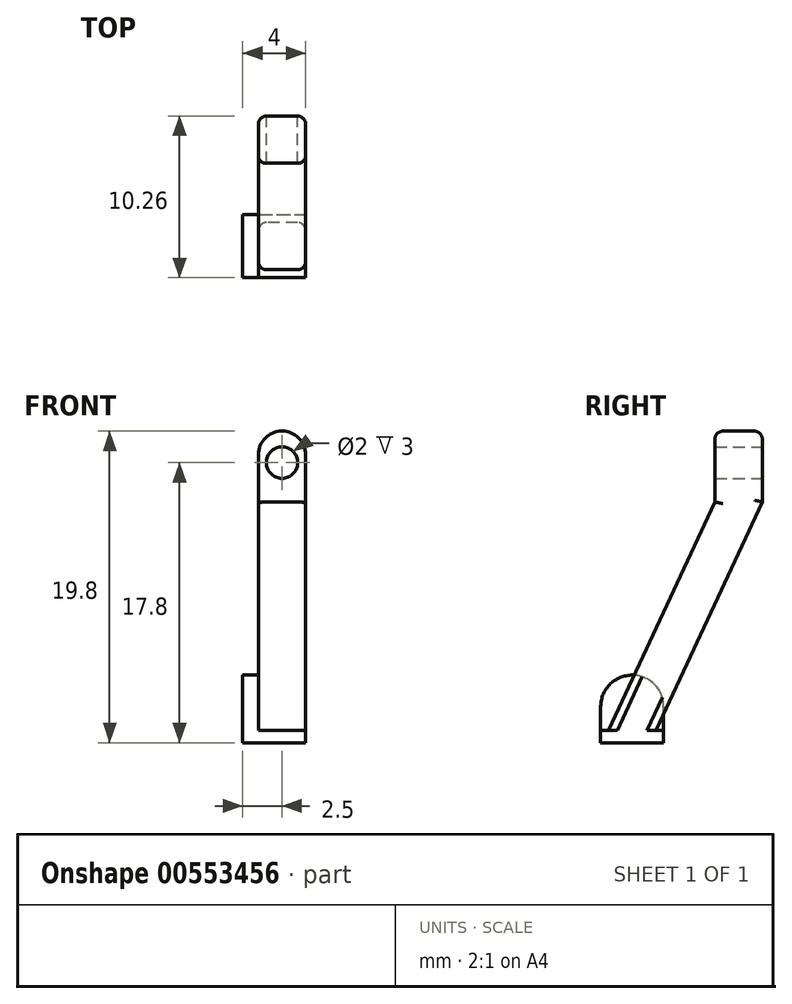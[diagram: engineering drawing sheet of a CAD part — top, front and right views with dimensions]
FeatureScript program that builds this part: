
annotation { "Feature Type Name" : "Feature", "Feature Type Description" : "" }
export const myFeature = defineFeature(function(context is Context, id is Id, definition is map)
    precondition{}
    {
        {
            var Q0;
            Q0=qCreatedBy(makeId("Top.planeOp"),FACE);
            var sketch = newSketch(context, id + "F0", { "sketchPlane" : qUnion([Q0])});
            skLineSegment(sketch, "E0.bottom", {"start": v(0, 0) * mm, "end": v(4, 0) * mm});
            skLineSegment(sketch, "E0.top", {"start": v(0, 4) * mm, "end": v(4, 4) * mm});
            skLineSegment(sketch, "E0.left", {"start": v(0, 0) * mm, "end": v(0, 4) * mm});
            skLineSegment(sketch, "E0.right", {"start": v(4, 0) * mm, "end": v(4, 4) * mm});
            skSolve(sketch);
        }
        {
            var Q0;
            Q0 = qSketchRegion(id + "F0", true);
            extrude(context, id + "F1", {"entities" : qUnion([Q0]), "depth" : 0.8 * mm, "offsetDistance" : 25 * mm});
        }
        {
            var Q0;
            Q0=qCreatedBy(makeId("Right.planeOp"),FACE);
            cPlane(context, id + "F2", {"entities" : qUnion([Q0]), "cplaneType" : CPlaneType.OFFSET, "offset" : 2.5 * mm, "width" : 150 * mm, "height" : 150 * mm});
        }
        {
            var Q0;
            Q0=qCreatedBy(id+"F2.planeOp",FACE);
            var sketch = newSketch(context, id + "F3", { "sketchPlane" : qUnion([Q0])});
            skLineSegment(sketch, "E1", {"start": v(3.5, 0.8) * mm, "end": v(10.26, 15.3) * mm});
            skLineSegment(sketch, "E2", {"start": v(7.26, 15.3) * mm, "end": v(0.5, 0.8) * mm});
            skLineSegment(sketch, "E3", {"start": v(0.5, 0.8) * mm, "end": v(3.5, 0.8) * mm});
            skLineSegment(sketch, "E4", {"start": v(7.26, 15.3) * mm, "end": v(7.26, 19.8) * mm});
            skLineSegment(sketch, "E5", {"start": v(7.26, 19.8) * mm, "end": v(10.26, 19.8) * mm});
            skLineSegment(sketch, "E6", {"start": v(10.26, 19.8) * mm, "end": v(10.26, 15.3) * mm});
            skLineSegment(sketch, "E7", {"start": v(7.26, 15.3) * mm, "end": v(15, 15.3) * mm, "construction": true});
            skSolve(sketch);
        }
        {
            var Q0;
            Q0 = qSketchRegion(id + "F3", true);
            extrude(context, id + "F4", {"entities" : qUnion([Q0]), "operationType" : NewBodyOperationType.ADD, "endBound" : BoundingType.SYMMETRIC, "depth" : 3 * mm, "offsetDistance" : 25 * mm});
        }
        {
            var Q0;
            Q0=makeQuery(id+"F4.opExtrude","SWEPT_FACE",FACE,{"disambiguationData":[OSD([sQuery(id+"F3.wireOp",EDGE,"E6")])]});
            var sketch = newSketch(context, id + "F5", { "sketchPlane" : qUnion([Q0])});
            skCircle(sketch, "E8", {"center": v(-2.5, 17.8) * mm, "radius": 1 * mm});
            skSolve(sketch);
        }
        {
            var Q0;
            Q0 = qSketchRegion(id + "F5", true);
            extrude(context, id + "F6", {"entities" : qUnion([Q0]), "operationType" : NewBodyOperationType.REMOVE, "endBound" : BoundingType.THROUGH_ALL, "oppositeDirection" : true, "depth" : 25 * mm, "offsetDistance" : 25 * mm});
        }
        {
            var Q0;
            Q0=makeQuery(id+"F4.opExtrude","CAP_EDGE",EDGE,{"disambiguationData":[OSD([sQuery(id+"F3.wireOp",EDGE,"E5")])],"isStart":true});
            var Q1;
            Q1=makeQuery(id+"F4.opExtrude","CAP_EDGE",EDGE,{"disambiguationData":[OSD([sQuery(id+"F3.wireOp",EDGE,"E5")])],"isStart":false});
            fillet(context, id + "F7", {"entities" : qUnion([Q0, Q1]), "radius" : 1.5 * mm, "tangentPropagation" : true, "allowEdgeOverflow" : false});
        }
        {
            var Q0;
            Q0=makeQuery(id+"F4.opExtrude","CAP_EDGE",EDGE,{"disambiguationData":[OSD([sQuery(id+"F3.wireOp",EDGE,"E1")])],"isStart":true});
            var Q1;
            Q1=makeQuery(id+"F4.opExtrude","CAP_EDGE",EDGE,{"disambiguationData":[OSD([sQuery(id+"F3.wireOp",EDGE,"E6")])],"isStart":true});
            var Q2;
            Q2=makeQuery(id+"F7.opFillet","BLEND_EDGE",EDGE,{"blendedFrom":[makeQuery(id+"F4.opExtrude","CAP_EDGE",EDGE,{"disambiguationData":[OSD([sQuery(id+"F3.wireOp",EDGE,"E5")])],"isStart":false}),makeQuery(id+"F4.opExtrude","SWEPT_FACE",FACE,{"disambiguationData":[OSD([sQuery(id+"F3.wireOp",EDGE,"E6")])]})],"blendedInto":[makeQuery(id+"F4.opExtrude","SWEPT_FACE",FACE,{"disambiguationData":[OSD([sQuery(id+"F3.wireOp",EDGE,"E6")])]})]});
            var Q3;
            Q3=makeQuery(id+"F4.opExtrude","CAP_EDGE",EDGE,{"disambiguationData":[OSD([sQuery(id+"F3.wireOp",EDGE,"E1")])],"isStart":false});
            var Q4;
            Q4=makeQuery(id+"F4.opExtrude","CAP_EDGE",EDGE,{"disambiguationData":[OSD([sQuery(id+"F3.wireOp",EDGE,"E2")])],"isStart":true});
            var Q5;
            Q5=makeQuery(id+"F4.opExtrude","CAP_EDGE",EDGE,{"disambiguationData":[OSD([sQuery(id+"F3.wireOp",EDGE,"E4")])],"isStart":true});
            var Q6;
            Q6=makeQuery(id+"F4.opExtrude","CAP_EDGE",EDGE,{"disambiguationData":[OSD([sQuery(id+"F3.wireOp",EDGE,"E2")])],"isStart":false});
            fillet(context, id + "F8", {"entities" : qUnion([Q0, Q1, Q2, Q3, Q4, Q5, Q6]), "radius" : 0.5 * mm, "tangentPropagation" : true, "allowEdgeOverflow" : false});
        }
        {
            var Q0;
            Q0=makeQuery(id+"F1.opExtrude","SWEPT_FACE",FACE,{"disambiguationData":[OSD([sQuery(id+"F0.wireOp",EDGE,"E0.left")])]});
            var sketch = newSketch(context, id + "F9", { "sketchPlane" : qUnion([Q0])});
            skLineSegment(sketch, "E9.bottom", {"start": v(-4, 0.8) * mm, "end": v(0, 0.8) * mm});
            skLineSegment(sketch, "E9.top", {"start": v(-2, 4.3) * mm, "end": v(-2, 4.3) * mm});
            skLineSegment(sketch, "E9.left", {"start": v(-4, 0.8) * mm, "end": v(-4, 2.3) * mm});
            skLineSegment(sketch, "E9.right", {"start": v(0, 0.8) * mm, "end": v(0, 2.3) * mm});
            skPoint(sketch, "E10.visualSharp", {"position": v(-4, 4.3) * mm});
            skArc(sketch, "E10.filletArc", {"start": v(-2, 4.3) * mm, "mid": v(-3.41, 3.71) * mm, "end": v(-4, 2.3) * mm});
            skPoint(sketch, "E11.visualSharp", {"position": v(0, 4.3) * mm});
            skArc(sketch, "E11.filletArc", {"start": v(0, 2.3) * mm, "mid": v(-0.59, 3.71) * mm, "end": v(-2, 4.3) * mm});
            skSolve(sketch);
        }
        {
            var Q0;
            Q0 = qSketchRegion(id + "F9", true);
            extrude(context, id + "F10", {"entities" : qUnion([Q0]), "operationType" : NewBodyOperationType.ADD, "oppositeDirection" : true, "depth" : 1 * mm, "offsetDistance" : 25 * mm});
        }
    });
